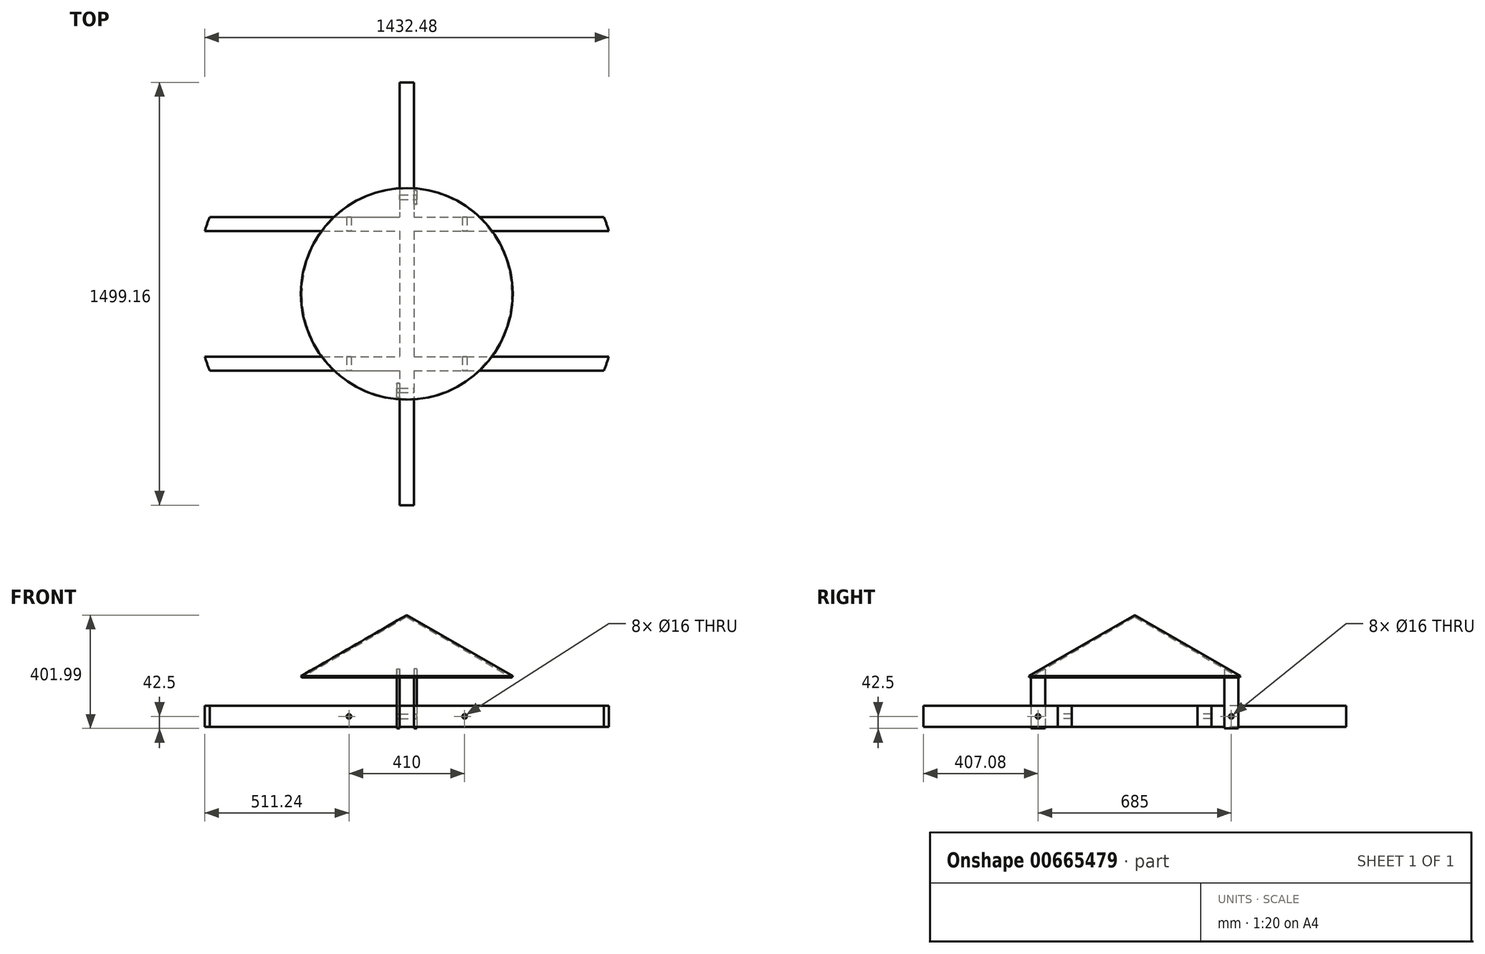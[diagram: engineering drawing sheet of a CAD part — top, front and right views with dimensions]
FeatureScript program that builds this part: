
annotation { "Feature Type Name" : "Feature", "Feature Type Description" : "" }
export const myFeature = defineFeature(function(context is Context, id is Id, definition is map)
    precondition{}
    {
        {
            assignVariable(context, id + "F0", {"name" : "MountFrameDepth", "anyValue" : 75});
        }
        {
            var Q0;
            Q0=qCreatedBy(makeId("Top.planeOp"),FACE);
            var sketch = newSketch(context, id + "F1", { "sketchPlane" : qUnion([Q0])});
            skCircle(sketch, "E0", {"center": v(0, 0) * mm, "radius": 750 * mm});
            skLineSegment(sketch, "E1.bottom", {"start": v(-25, 749.58) * mm, "end": v(25, 749.58) * mm});
            skLineSegment(sketch, "E1.top", {"start": v(-25, -749.58) * mm, "end": v(25, -749.58) * mm});
            skLineSegment(sketch, "E1.left", {"start": v(-25, 749.58) * mm, "end": v(-25, -749.58) * mm});
            skLineSegment(sketch, "E1.right", {"start": v(25, 749.58) * mm, "end": v(25, -749.58) * mm});
            skLineSegment(sketch, "E2.bottom", {"start": v(-698.74, 272.5) * mm, "end": v(698.74, 272.5) * mm});
            skLineSegment(sketch, "E2.top", {"start": v(-716.24, 222.5) * mm, "end": v(716.24, 222.5) * mm});
            skLineSegment(sketch, "E3.bottom", {"start": v(-698.74, -272.5) * mm, "end": v(698.74, -272.5) * mm});
            skLineSegment(sketch, "E3.top", {"start": v(-716.24, -222.5) * mm, "end": v(716.24, -222.5) * mm});
            skLineSegment(sketch, "E4", {"start": v(-205, 342.5) * mm, "end": v(205, 342.5) * mm, "construction": true});
            skLineSegment(sketch, "E5", {"start": v(-205, -342.5) * mm, "end": v(205, -342.5) * mm, "construction": true});
            skLineSegment(sketch, "E6", {"start": v(205, 342.5) * mm, "end": v(205, -342.5) * mm, "construction": true});
            skLineSegment(sketch, "E7", {"start": v(-205, 342.5) * mm, "end": v(-205, -342.5) * mm, "construction": true});
            skLineSegment(sketch, "E8.bottom", {"start": v(180, 272.5) * mm, "end": v(230, 272.5) * mm});
            skLineSegment(sketch, "E8.top", {"start": v(180, 282.5) * mm, "end": v(230, 282.5) * mm});
            skLineSegment(sketch, "E8.left", {"start": v(180, 272.5) * mm, "end": v(180, 282.5) * mm});
            skLineSegment(sketch, "E8.right", {"start": v(230, 272.5) * mm, "end": v(230, 282.5) * mm});
            skLineSegment(sketch, "E9.bottom", {"start": v(180, -272.5) * mm, "end": v(230, -272.5) * mm});
            skLineSegment(sketch, "E9.top", {"start": v(180, -282.5) * mm, "end": v(230, -282.5) * mm});
            skLineSegment(sketch, "E9.left", {"start": v(180, -272.5) * mm, "end": v(180, -282.5) * mm});
            skLineSegment(sketch, "E9.right", {"start": v(230, -272.5) * mm, "end": v(230, -282.5) * mm});
            skLineSegment(sketch, "E10.bottom", {"start": v(-230, -272.5) * mm, "end": v(-180, -272.5) * mm});
            skLineSegment(sketch, "E10.top", {"start": v(-230, -282.5) * mm, "end": v(-180, -282.5) * mm});
            skLineSegment(sketch, "E10.left", {"start": v(-230, -272.5) * mm, "end": v(-230, -282.5) * mm});
            skLineSegment(sketch, "E10.right", {"start": v(-180, -272.5) * mm, "end": v(-180, -282.5) * mm});
            skLineSegment(sketch, "E11.bottom", {"start": v(-230, 272.5) * mm, "end": v(-180, 272.5) * mm});
            skLineSegment(sketch, "E11.top", {"start": v(-230, 282.5) * mm, "end": v(-180, 282.5) * mm});
            skLineSegment(sketch, "E11.left", {"start": v(-230, 272.5) * mm, "end": v(-230, 282.5) * mm});
            skLineSegment(sketch, "E11.right", {"start": v(-180, 272.5) * mm, "end": v(-180, 282.5) * mm});
            skLineSegment(sketch, "E12.bottom", {"start": v(25, 367.5) * mm, "end": v(35, 367.5) * mm});
            skLineSegment(sketch, "E12.top", {"start": v(25, 317.5) * mm, "end": v(35, 317.5) * mm});
            skLineSegment(sketch, "E12.left", {"start": v(25, 367.5) * mm, "end": v(25, 317.5) * mm});
            skLineSegment(sketch, "E12.right", {"start": v(35, 367.5) * mm, "end": v(35, 317.5) * mm});
            skLineSegment(sketch, "E13.bottom", {"start": v(-25, -317.5) * mm, "end": v(-35, -317.5) * mm});
            skLineSegment(sketch, "E13.top", {"start": v(-25, -367.5) * mm, "end": v(-35, -367.5) * mm});
            skLineSegment(sketch, "E13.left", {"start": v(-25, -317.5) * mm, "end": v(-25, -367.5) * mm});
            skLineSegment(sketch, "E13.right", {"start": v(-35, -317.5) * mm, "end": v(-35, -367.5) * mm});
            skSolve(sketch);
        }
        {
            var Q0;
            {var subQ0=sQuery(id+"F1.wireOp",EDGE,"E1.top");Q0=makeQuery(id+"F1.imprint","IMPRINT",FACE,{"disambiguationData":[TD([[makeQuery(id+"F1.imprint","IMPRINT",EDGE,{"derivedFrom":subQ0}),1.0]])]});}
            var Q1;
            {var subQ0=sQuery(id+"F1.wireOp",EDGE,"E2.bottom");var subQ1=sQuery(id+"F1.wireOp",EDGE,"E1.left");var subQ2=makeQuery(id+"F1.imprint","INTERSECT",VERTEX,{"derivedFrom":[subQ1,subQ0]});Q1=makeQuery(id+"F1.imprint","IMPRINT",FACE,{"disambiguationData":[TD([[makeQuery(id+"F1.imprint","IMPRINT",EDGE,{"disambiguationData":[TD([[subQ2,-1.0]])],"derivedFrom":subQ1}),1.0]])]});}
            var Q2;
            {var subQ0=sQuery(id+"F1.wireOp",EDGE,"E2.bottom");var subQ1=sQuery(id+"F1.wireOp",EDGE,"E0");var subQ2=makeQuery(id+"F1.imprint","INTERSECT",VERTEX,{"disambiguationData":[OD(0.0)],"derivedFrom":[subQ1,subQ0]});Q2=makeQuery(id+"F1.imprint","IMPRINT",FACE,{"disambiguationData":[TD([[makeQuery(id+"F1.imprint","IMPRINT",EDGE,{"disambiguationData":[TD([[subQ2,-1.0]])],"derivedFrom":subQ1}),1.0]])]});}
            var Q3;
            {var subQ0=sQuery(id+"F1.wireOp",EDGE,"E2.bottom");var subQ1=sQuery(id+"F1.wireOp",EDGE,"E0");var subQ2=makeQuery(id+"F1.imprint","INTERSECT",VERTEX,{"disambiguationData":[OD(1.0)],"derivedFrom":[subQ1,subQ0]});Q3=makeQuery(id+"F1.imprint","IMPRINT",FACE,{"disambiguationData":[TD([[makeQuery(id+"F1.imprint","IMPRINT",EDGE,{"disambiguationData":[TD([[subQ2,1.0]])],"derivedFrom":subQ1}),1.0]])]});}
            var Q4;
            {var subQ0=sQuery(id+"F1.wireOp",EDGE,"E1.bottom");Q4=makeQuery(id+"F1.imprint","IMPRINT",FACE,{"disambiguationData":[TD([[makeQuery(id+"F1.imprint","IMPRINT",EDGE,{"derivedFrom":subQ0}),-1.0]])]});}
            var Q5;
            {var subQ0=sQuery(id+"F1.wireOp",EDGE,"E2.top");var subQ1=sQuery(id+"F1.wireOp",EDGE,"E1.left");var subQ2=makeQuery(id+"F1.imprint","INTERSECT",VERTEX,{"derivedFrom":[subQ1,subQ0]});Q5=makeQuery(id+"F1.imprint","IMPRINT",FACE,{"disambiguationData":[TD([[makeQuery(id+"F1.imprint","IMPRINT",EDGE,{"disambiguationData":[TD([[subQ2,-1.0]])],"derivedFrom":subQ1}),1.0]])]});}
            var Q6;
            {var subQ0=sQuery(id+"F1.wireOp",EDGE,"E3.bottom");var subQ1=sQuery(id+"F1.wireOp",EDGE,"E0");var subQ2=makeQuery(id+"F1.imprint","INTERSECT",VERTEX,{"disambiguationData":[OD(0.0)],"derivedFrom":[subQ1,subQ0]});Q6=makeQuery(id+"F1.imprint","IMPRINT",FACE,{"disambiguationData":[TD([[makeQuery(id+"F1.imprint","IMPRINT",EDGE,{"disambiguationData":[TD([[subQ2,1.0]])],"derivedFrom":subQ1}),1.0]])]});}
            var Q7;
            {var subQ0=sQuery(id+"F1.wireOp",EDGE,"E3.top");var subQ1=sQuery(id+"F1.wireOp",EDGE,"E1.left");var subQ2=makeQuery(id+"F1.imprint","INTERSECT",VERTEX,{"derivedFrom":[subQ1,subQ0]});Q7=makeQuery(id+"F1.imprint","IMPRINT",FACE,{"disambiguationData":[TD([[makeQuery(id+"F1.imprint","IMPRINT",EDGE,{"disambiguationData":[TD([[subQ2,-1.0]])],"derivedFrom":subQ1}),1.0]])]});}
            var Q8;
            {var subQ0=sQuery(id+"F1.wireOp",EDGE,"E3.bottom");var subQ1=sQuery(id+"F1.wireOp",EDGE,"E0");var subQ2=makeQuery(id+"F1.imprint","INTERSECT",VERTEX,{"disambiguationData":[OD(1.0)],"derivedFrom":[subQ1,subQ0]});Q8=makeQuery(id+"F1.imprint","IMPRINT",FACE,{"disambiguationData":[TD([[makeQuery(id+"F1.imprint","IMPRINT",EDGE,{"disambiguationData":[TD([[subQ2,-1.0]])],"derivedFrom":subQ1}),1.0]])]});}
            extrude(context, id + "F2", {"entities" : qUnion([Q0, Q1, Q2, Q3, Q4, Q5, Q6, Q7, Q8]), "oppositeDirection" : true, "depth" : (getVariable(context, 'MountFrameDepth')) * mm, "offsetDistance" : 25 * mm});
        }
        {
            var Q0;
            Q0=qCreatedBy(makeId("Front.planeOp"),FACE);
            var sketch = newSketch(context, id + "F3", { "sketchPlane" : qUnion([Q0])});
            skLineSegment(sketch, "E14", {"start": v(0, 107.95) * mm, "end": v(0, -61.22) * mm, "construction": true});
            skLineSegment(sketch, "E15", {"start": v(-372.5, 100) * mm, "end": v(0, 315.06) * mm});
            skLineSegment(sketch, "E16", {"start": v(0, 315.06) * mm, "end": v(0, 322) * mm});
            skLineSegment(sketch, "E17", {"start": v(0, 322) * mm, "end": v(-375.5, 105.2) * mm});
            skLineSegment(sketch, "E18", {"start": v(-375.5, 105.2) * mm, "end": v(-372.5, 100) * mm});
            skLineSegment(sketch, "E19", {"start": v(-205, 197.4) * mm, "end": v(-205, -189.83) * mm, "construction": true});
            skLineSegment(sketch, "E20", {"start": v(205, 197.4) * mm, "end": v(205, -189.83) * mm, "construction": true});
            skLineSegment(sketch, "E21", {"start": v(-761.26, -37.5) * mm, "end": v(754.26, -37.5) * mm, "construction": true});
            skCircle(sketch, "E22", {"center": v(-205, -37.5) * mm, "radius": 8 * mm});
            skCircle(sketch, "E23", {"center": v(205, -37.5) * mm, "radius": 8 * mm});
            skLineSegment(sketch, "E24", {"start": v(-438.3, 100) * mm, "end": v(11.55, 100) * mm, "construction": true});
            skSolve(sketch);
        }
        {
            var Q0;
            Q0=makeQuery(id+"F3.imprint","IMPRINT",FACE,{"disambiguationData":[TD([[makeQuery(id+"F3.imprint","IMPRINT",EDGE,{"derivedFrom":sQuery(id+"F3.wireOp",EDGE,"E15")}),1.0]])]});
            var Q1;
            Q1=sQuery(id+"F3.wireOp",EDGE,"E14");
            revolve(context, id + "F4", {"entities" : qUnion([Q0]), "axis" : qUnion([Q1]), "revolveType" : RevolveType.FULL});
        }
        {
            var Q0;
            Q0=makeQuery(id+"F1.imprint","IMPRINT",FACE,{"disambiguationData":[TD([[makeQuery(id+"F1.imprint","IMPRINT",EDGE,{"derivedFrom":sQuery(id+"F1.wireOp",EDGE,"E13.bottom")}),1.0]])]});
            var Q1;
            Q1=makeQuery(id+"F1.imprint","IMPRINT",FACE,{"disambiguationData":[TD([[makeQuery(id+"F1.imprint","IMPRINT",EDGE,{"derivedFrom":sQuery(id+"F1.wireOp",EDGE,"E9.bottom")}),-1.0]])]});
            var Q2;
            Q2=makeQuery(id+"F1.imprint","IMPRINT",FACE,{"disambiguationData":[TD([[makeQuery(id+"F1.imprint","IMPRINT",EDGE,{"derivedFrom":sQuery(id+"F1.wireOp",EDGE,"E10.bottom")}),-1.0]])]});
            var Q3;
            Q3=makeQuery(id+"F1.imprint","IMPRINT",FACE,{"disambiguationData":[TD([[makeQuery(id+"F1.imprint","IMPRINT",EDGE,{"derivedFrom":sQuery(id+"F1.wireOp",EDGE,"E12.bottom")}),-1.0]])]});
            var Q4;
            Q4=makeQuery(id+"F1.imprint","IMPRINT",FACE,{"disambiguationData":[TD([[makeQuery(id+"F1.imprint","IMPRINT",EDGE,{"derivedFrom":sQuery(id+"F1.wireOp",EDGE,"E8.bottom")}),1.0]])]});
            var Q5;
            Q5=makeQuery(id+"F1.imprint","IMPRINT",FACE,{"disambiguationData":[TD([[makeQuery(id+"F1.imprint","IMPRINT",EDGE,{"derivedFrom":sQuery(id+"F1.wireOp",EDGE,"E11.bottom")}),1.0]])]});
            extrude(context, id + "F5", {"entities" : qUnion([Q0, Q1, Q2, Q3, Q4, Q5]), "endBound" : BoundingType.UP_TO_NEXT, "depth" : 25 * mm, "offsetDistance" : 25 * mm, "hasSecondDirection" : true, "secondDirectionOppositeDirection" : true, "secondDirectionDepth" : 80 * mm});
        }
        {
            var Q0;
            Q0=makeQuery(id+"F3.imprint","IMPRINT",FACE,{"disambiguationData":[TD([[makeQuery(id+"F3.imprint","IMPRINT",EDGE,{"derivedFrom":sQuery(id+"F3.wireOp",EDGE,"E22")}),1.0]])]});
            var Q1;
            Q1=makeQuery(id+"F3.imprint","IMPRINT",FACE,{"disambiguationData":[TD([[makeQuery(id+"F3.imprint","IMPRINT",EDGE,{"derivedFrom":sQuery(id+"F3.wireOp",EDGE,"E23")}),1.0]])]});
            extrude(context, id + "F6", {"entities" : qUnion([Q0, Q1]), "operationType" : NewBodyOperationType.REMOVE, "endBound" : BoundingType.THROUGH_ALL, "oppositeDirection" : true, "depth" : 25 * mm, "offsetDistance" : 25 * mm, "hasSecondDirection" : true, "secondDirectionBound" : SecondDirectionBoundingType.THROUGH_ALL, "secondDirectionOppositeDirection" : false, "secondDirectionDepth" : 25 * mm});
        }
        {
            var Q0;
            Q0=qCreatedBy(makeId("Right.planeOp"),FACE);
            var sketch = newSketch(context, id + "F7", { "sketchPlane" : qUnion([Q0])});
            skLineSegment(sketch, "E25", {"start": v(-805.78, -37.5) * mm, "end": v(807.61, -37.5) * mm, "construction": true});
            skLineSegment(sketch, "E26", {"start": v(-342.5, 108.03) * mm, "end": v(-342.5, -137.38) * mm, "construction": true});
            skLineSegment(sketch, "E27", {"start": v(342.5, 108.03) * mm, "end": v(342.5, -137.38) * mm, "construction": true});
            skCircle(sketch, "E28", {"center": v(-342.5, -37.5) * mm, "radius": 8 * mm});
            skCircle(sketch, "E29", {"center": v(342.5, -37.5) * mm, "radius": 8 * mm});
            skSolve(sketch);
        }
        {
            var Q0;
            Q0=makeQuery(id+"F7.imprint","IMPRINT",FACE,{"disambiguationData":[TD([[makeQuery(id+"F7.imprint","IMPRINT",EDGE,{"derivedFrom":sQuery(id+"F7.wireOp",EDGE,"E28")}),1.0]])]});
            var Q1;
            Q1=makeQuery(id+"F7.imprint","IMPRINT",FACE,{"disambiguationData":[TD([[makeQuery(id+"F7.imprint","IMPRINT",EDGE,{"derivedFrom":sQuery(id+"F7.wireOp",EDGE,"E29")}),1.0]])]});
            extrude(context, id + "F8", {"entities" : qUnion([Q0, Q1]), "operationType" : NewBodyOperationType.REMOVE, "endBound" : BoundingType.THROUGH_ALL, "oppositeDirection" : true, "depth" : 25 * mm, "offsetDistance" : 25 * mm, "hasSecondDirection" : true, "secondDirectionBound" : SecondDirectionBoundingType.THROUGH_ALL, "secondDirectionOppositeDirection" : false, "secondDirectionDepth" : 25 * mm});
        }
    });
